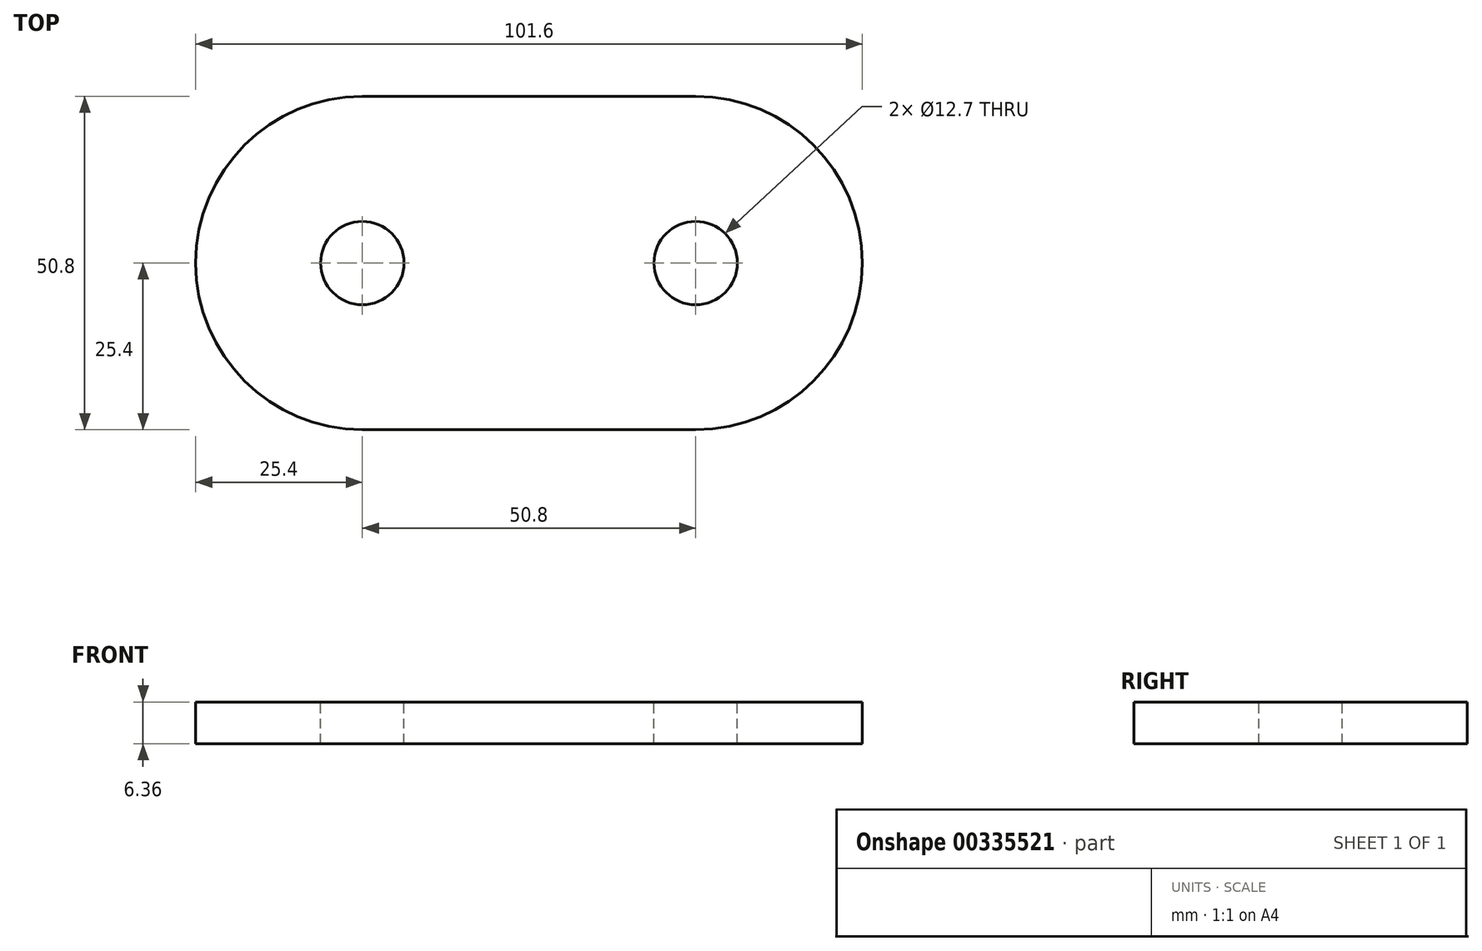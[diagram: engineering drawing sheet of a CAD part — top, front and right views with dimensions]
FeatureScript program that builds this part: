
annotation { "Feature Type Name" : "Feature", "Feature Type Description" : "" }
export const myFeature = defineFeature(function(context is Context, id is Id, definition is map)
    precondition{}
    {
        {
            var Q0;
            Q0=qCreatedBy(makeId("Top.planeOp"),FACE);
            var sketch = newSketch(context, id + "F0", { "sketchPlane" : qUnion([Q0])});
            skLineSegment(sketch, "E0.bottom", {"start": v(50.8, -25.4) * mm, "end": v(-50.8, -25.4) * mm});
            skLineSegment(sketch, "E0.top", {"start": v(50.8, 25.4) * mm, "end": v(-50.8, 25.4) * mm});
            skLineSegment(sketch, "E0.left", {"start": v(50.8, -25.4) * mm, "end": v(50.8, 25.4) * mm});
            skLineSegment(sketch, "E0.right", {"start": v(-50.8, -25.4) * mm, "end": v(-50.8, 25.4) * mm});
            skPoint(sketch, "E0.middle", {"position": v(0, 0) * mm});
            skSolve(sketch);
        }
        {
            var Q0;
            Q0 = qSketchRegion(id + "F0", true);
            extrude(context, id + "F1", {"entities" : qUnion([Q0]), "endBound" : BoundingType.SYMMETRIC, "depth" : 6.35 * mm});
        }
        {
            var Q0;
            Q0=makeQuery(id+"F1.opExtrude","SWEPT_EDGE",EDGE,{"disambiguationData":[OSD([sQuery(id+"F0.wireOp",EDGE,"E0.bottom"),sQuery(id+"F0.wireOp",EDGE,"E0.right")])]});
            var Q1;
            Q1=makeQuery(id+"F1.opExtrude","SWEPT_EDGE",EDGE,{"disambiguationData":[OSD([sQuery(id+"F0.wireOp",EDGE,"E0.bottom"),sQuery(id+"F0.wireOp",EDGE,"E0.left")])]});
            var Q2;
            Q2=makeQuery(id+"F1.opExtrude","SWEPT_EDGE",EDGE,{"disambiguationData":[OSD([sQuery(id+"F0.wireOp",EDGE,"E0.top"),sQuery(id+"F0.wireOp",EDGE,"E0.left")])]});
            var Q3;
            Q3=makeQuery(id+"F1.opExtrude","SWEPT_EDGE",EDGE,{"disambiguationData":[OSD([sQuery(id+"F0.wireOp",EDGE,"E0.top"),sQuery(id+"F0.wireOp",EDGE,"E0.right")])]});
            fillet(context, id + "F2", {"entities" : qUnion([Q0, Q1, Q2, Q3]), "radius" : 25.4 * mm, "tangentPropagation" : true, "allowEdgeOverflow" : false});
        }
        {
            var Q0;
            Q0=makeQuery(id+"F1.opExtrude","CAP_FACE",FACE,{"disambiguationData":[OSD([sQuery(id+"F0.wireOp",EDGE,"E0.bottom"),sQuery(id+"F0.wireOp",EDGE,"E0.top"),sQuery(id+"F0.wireOp",EDGE,"E0.left"),sQuery(id+"F0.wireOp",EDGE,"E0.right")])],"isStart":false});
            var sketch = newSketch(context, id + "F3", { "sketchPlane" : qUnion([Q0])});
            skPoint(sketch, "E1", {"position": v(25.4, 0) * mm});
            skPoint(sketch, "E2", {"position": v(-25.4, 0) * mm});
            skSolve(sketch);
        }
        {
            var Q0;
            Q0=sQuery(id+"F3.wireOp",VERTEX,"E1");
            var Q1;
            Q1=sQuery(id+"F3.wireOp",VERTEX,"E2");
            var Q2;
            Q2=makeQuery(id+"F1.opExtrude","SWEPT_BODY",BODY,{"disambiguationData":[OSD([sQuery(id+"F0.wireOp",EDGE,"E0.bottom"),sQuery(id+"F0.wireOp",EDGE,"E0.top"),sQuery(id+"F0.wireOp",EDGE,"E0.left"),sQuery(id+"F0.wireOp",EDGE,"E0.right")])]});
            hole(context, id + "F4", {"style" : HoleStyle.SIMPLE, "endStyle" : HoleEndStyle.THROUGH, "holeDiameter" : 12.7 * mm, "tappedDepth" : 12.7 * mm, "tapClearance" : 3, "locations" : qUnion([Q0, Q1]), "scope" : qUnion([Q2])});
        }
    });
